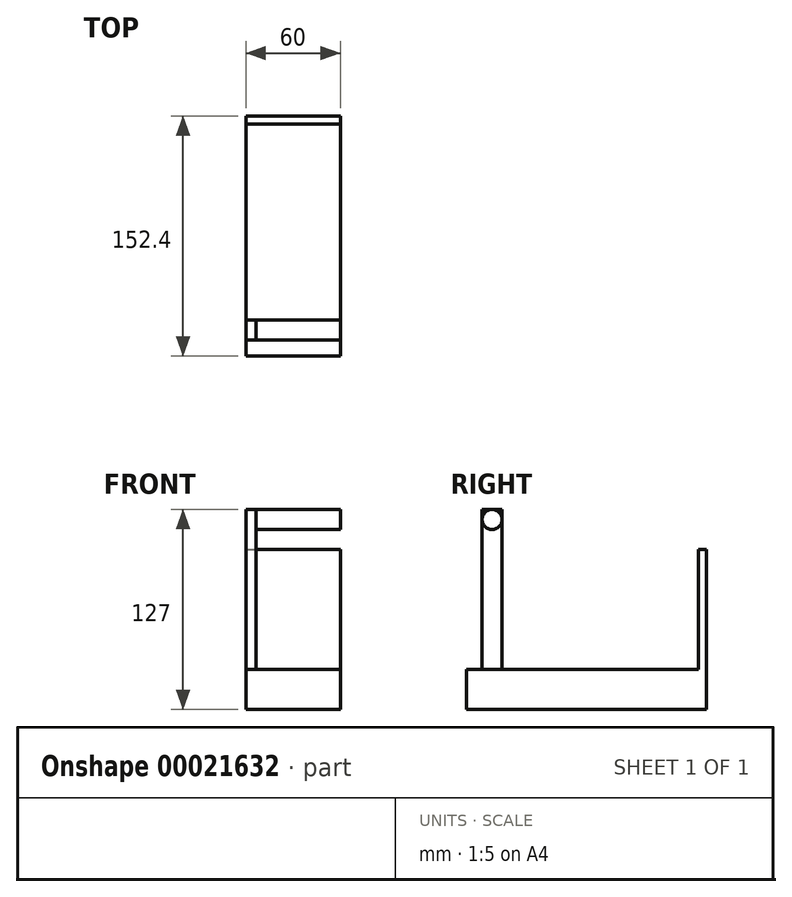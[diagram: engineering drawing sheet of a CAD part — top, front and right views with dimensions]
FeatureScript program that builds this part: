
annotation { "Feature Type Name" : "Feature", "Feature Type Description" : "" }
export const myFeature = defineFeature(function(context is Context, id is Id, definition is map)
    precondition{}
    {
        {
            var Q0;
            Q0=qCreatedBy(makeId("Top.planeOp"),FACE);
            var sketch = newSketch(context, id + "F0", { "sketchPlane" : qUnion([Q0])});
            skLineSegment(sketch, "E0.bottom", {"start": v(-60, 121.25) * mm, "end": v(0, 121.25) * mm});
            skLineSegment(sketch, "E0.top", {"start": v(-60, -31.15) * mm, "end": v(0, -31.15) * mm});
            skLineSegment(sketch, "E0.left", {"start": v(-60, 121.25) * mm, "end": v(-60, -31.15) * mm});
            skLineSegment(sketch, "E0.right", {"start": v(0, 121.25) * mm, "end": v(0, -31.15) * mm});
            skLineSegment(sketch, "E1", {"start": v(-60, 116.25) * mm, "end": v(0, 116.25) * mm});
            skPoint(sketch, "E2", {"position": v(-60, -21.15) * mm});
            skPoint(sketch, "E3", {"position": v(-60, -8.45) * mm});
            skLineSegment(sketch, "E4", {"start": v(-60, -8.45) * mm, "end": v(-53.65, -8.45) * mm});
            skLineSegment(sketch, "E5", {"start": v(-60, -21.15) * mm, "end": v(-53.65, -21.15) * mm});
            skPoint(sketch, "E6", {"position": v(-53.65, -8.45) * mm});
            skLineSegment(sketch, "E7", {"start": v(-53.65, -8.45) * mm, "end": v(-53.65, -21.15) * mm});
            skPoint(sketch, "E8.orphan", {"position": v(0, -8.45) * mm});
            skPoint(sketch, "E9.orphan", {"position": v(0, -21.15) * mm});
            skSolve(sketch);
        }
        {
            var Q0;
            {var subQ2=sQuery(id+"F0.wireOp",EDGE,"E0.bottom");Q0=makeQuery(id+"F0.imprint","IMPRINT",FACE,{"disambiguationData":[TD([[makeQuery(id+"F0.imprint","IMPRINT",EDGE,{"derivedFrom":subQ2}),-1.0]])]});}
            var Q1;
            {var subQ4=sQuery(id+"F0.wireOp",EDGE,"E0.top");Q1=makeQuery(id+"F0.imprint","IMPRINT",FACE,{"disambiguationData":[TD([[makeQuery(id+"F0.imprint","IMPRINT",EDGE,{"derivedFrom":subQ4}),1.0]])]});}
            var Q2;
            {var subQ1=sQuery(id+"F0.wireOp",EDGE,"E4");Q2=makeQuery(id+"F0.imprint","IMPRINT",FACE,{"disambiguationData":[TD([[makeQuery(id+"F0.imprint","IMPRINT",EDGE,{"derivedFrom":subQ1}),-1.0]])]});}
            extrude(context, id + "F1", {"entities" : qUnion([Q0, Q1, Q2]), "oppositeDirection" : true, "depth" : 25.4 * mm});
        }
        {
            var Q0;
            {var subQ1=sQuery(id+"F0.wireOp",EDGE,"E4");Q0=makeQuery(id+"F0.imprint","IMPRINT",FACE,{"disambiguationData":[TD([[makeQuery(id+"F0.imprint","IMPRINT",EDGE,{"derivedFrom":subQ1}),-1.0]])]});}
            extrude(context, id + "F2", {"entities" : qUnion([Q0]), "operationType" : NewBodyOperationType.ADD, "depth" : 101.6 * mm});
        }
        {
            var Q0;
            {var subQ2=sQuery(id+"F0.wireOp",EDGE,"E0.bottom");Q0=makeQuery(id+"F0.imprint","IMPRINT",FACE,{"disambiguationData":[TD([[makeQuery(id+"F0.imprint","IMPRINT",EDGE,{"derivedFrom":subQ2}),-1.0]])]});}
            extrude(context, id + "F3", {"entities" : qUnion([Q0]), "operationType" : NewBodyOperationType.ADD, "depth" : 76.2 * mm});
        }
        {
            var Q0;
            Q0=qCreatedBy(makeId("Right.planeOp"),FACE);
            var sketch = newSketch(context, id + "F4", { "sketchPlane" : qUnion([Q0])});
            skLineSegment(sketch, "E10.0.0", {"start": v(-21.15, 0) * mm, "end": v(-8.45, 0) * mm});
            skLineSegment(sketch, "E10.0.1", {"start": v(-8.45, 0) * mm, "end": v(-8.45, 101.6) * mm});
            skLineSegment(sketch, "E10.0.2", {"start": v(-8.45, 101.6) * mm, "end": v(-21.15, 101.6) * mm});
            skLineSegment(sketch, "E10.0.3", {"start": v(-21.15, 101.6) * mm, "end": v(-21.15, 88.9) * mm});
            skPoint(sketch, "E11", {"position": v(-21.15, 88.9) * mm});
            skPoint(sketch, "E12", {"position": v(-14.8, 101.6) * mm});
            skPoint(sketch, "E13", {"position": v(-21.15, 95.25) * mm});
            skCircle(sketch, "E14", {"center": v(-14.8, 95.25) * mm, "radius": 6.35 * mm});
            skSolve(sketch);
        }
        {
            var Q0;
            {var subQ0=sQuery(id+"F4.wireOp",EDGE,"E14");var subQ2=makeQuery(id+"F4.imprint","INTERSECT",VERTEX,{"derivedFrom":[sQuery(id+"F4.wireOp",EDGE,"E10.0.1"),subQ0]});Q0=makeQuery(id+"F4.imprint","IMPRINT",FACE,{"disambiguationData":[TD([[makeQuery(id+"F4.imprint","IMPRINT",EDGE,{"disambiguationData":[TD([[subQ2,-1.0]])],"derivedFrom":subQ0}),1.0]])]});}
            var Q1;
            Q1=makeQuery(id+"F2.opExtrude","SWEPT_FACE",FACE,{"disambiguationData":[OSD([sQuery(id+"F0.wireOp",EDGE,"E7")])]});
            extrude(context, id + "F5", {"entities" : qUnion([Q0]), "operationType" : NewBodyOperationType.ADD, "endBound" : BoundingType.UP_TO_SURFACE, "oppositeDirection" : true, "endBoundEntityFace" : qUnion([Q1]), "depth" : 25.4 * mm});
        }
    });
